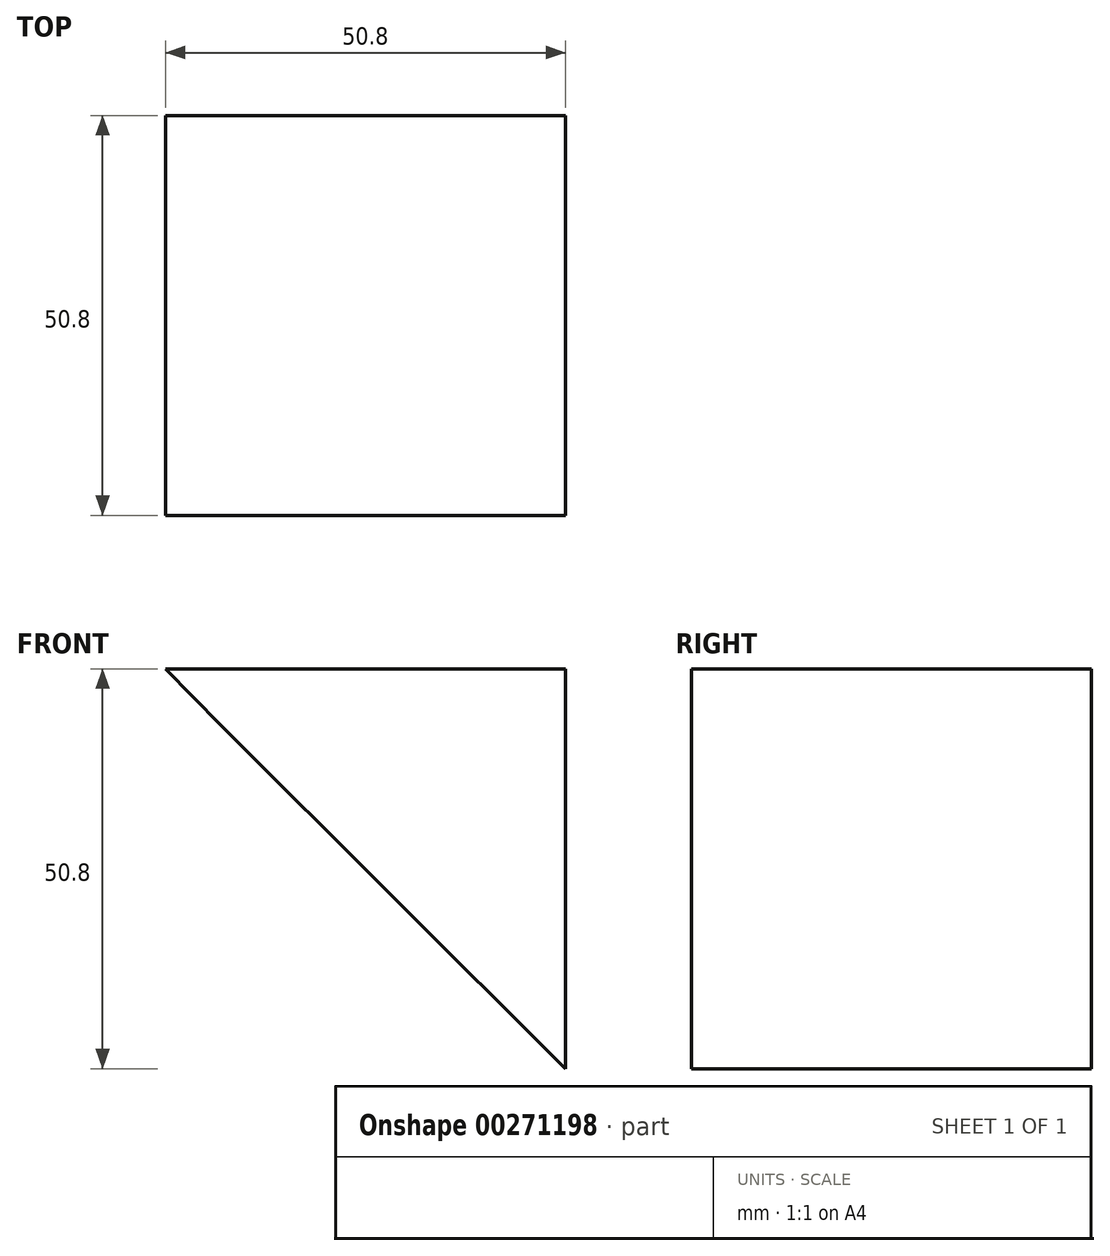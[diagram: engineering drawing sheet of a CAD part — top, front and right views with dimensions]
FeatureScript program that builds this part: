
annotation { "Feature Type Name" : "Feature", "Feature Type Description" : "" }
export const myFeature = defineFeature(function(context is Context, id is Id, definition is map)
    precondition{}
    {
        {
            var Q0;
            Q0=qCreatedBy(makeId("Front.planeOp"),FACE);
            var sketch = newSketch(context, id + "F0", { "sketchPlane" : qUnion([Q0])});
            skLineSegment(sketch, "E0.bottom", {"start": v(0, 0) * mm, "end": v(-50.8, 0) * mm});
            skLineSegment(sketch, "E0.top", {"start": v(0, 50.8) * mm, "end": v(-50.8, 50.8) * mm});
            skLineSegment(sketch, "E0.left", {"start": v(0, 0) * mm, "end": v(0, 50.8) * mm});
            skLineSegment(sketch, "E0.right", {"start": v(-50.8, 0) * mm, "end": v(-50.8, 50.8) * mm});
            skSolve(sketch);
        }
        {
            var Q0;
            Q0=makeQuery(id+"F0.imprint","IMPRINT",FACE,{"disambiguationData":[TD([[makeQuery(id+"F0.imprint","IMPRINT",EDGE,{"derivedFrom":sQuery(id+"F0.wireOp",EDGE,"E0.bottom")}),-1.0]])]});
            extrude(context, id + "F1", {"entities" : qUnion([Q0]), "depth" : 50.8 * mm});
        }
        {
            var Q0;
            Q0=makeQuery(id+"F1.opExtrude","CAP_FACE",FACE,{"disambiguationData":[OSD([sQuery(id+"F0.wireOp",EDGE,"E0.bottom"),sQuery(id+"F0.wireOp",EDGE,"E0.top"),sQuery(id+"F0.wireOp",EDGE,"E0.left"),sQuery(id+"F0.wireOp",EDGE,"E0.right")])],"isStart":false});
            var sketch = newSketch(context, id + "F2", { "sketchPlane" : qUnion([Q0])});
            skLineSegment(sketch, "E1", {"start": v(-50.8, 50.8) * mm, "end": v(-43.8, 43.7) * mm});
            skLineSegment(sketch, "E2", {"start": v(-43.8, 43.7) * mm, "end": v(0, 0) * mm});
            skSolve(sketch);
        }
        {
            var Q0;
            Q0=makeQuery(id+"F2.imprint","IMPRINT",FACE,{"disambiguationData":[TD([[makeQuery(id+"F2.imprint","IMPRINT",EDGE,{"derivedFrom":sQuery(id+"F2.wireOp",EDGE,"E1")}),-1.0]])]});
            extrude(context, id + "F3", {"entities" : qUnion([Q0]), "operationType" : NewBodyOperationType.REMOVE, "oppositeDirection" : true, "depth" : 50.8 * mm});
        }
    });
